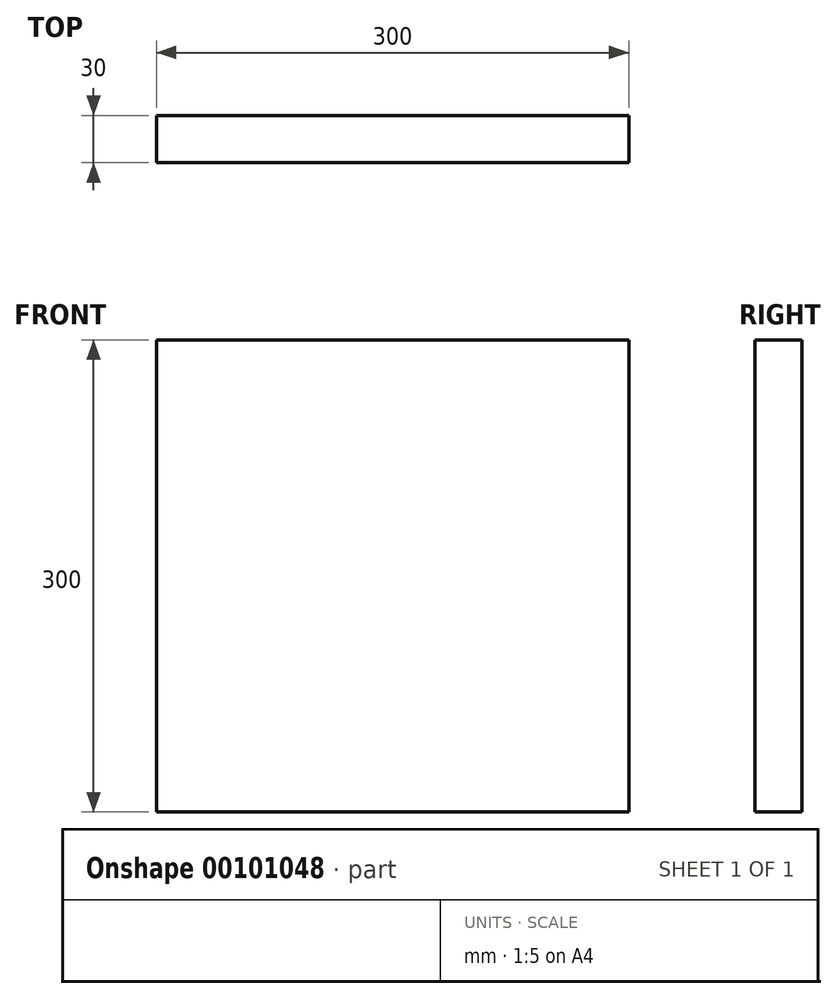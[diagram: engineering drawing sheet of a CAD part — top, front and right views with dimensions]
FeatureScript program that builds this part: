
annotation { "Feature Type Name" : "Feature", "Feature Type Description" : "" }
export const myFeature = defineFeature(function(context is Context, id is Id, definition is map)
    precondition{}
    {
        {
            var Q0;
            Q0=qCreatedBy(makeId("Front.planeOp"),FACE);
            var sketch = newSketch(context, id + "F0", { "sketchPlane" : qUnion([Q0])});
            skLineSegment(sketch, "E0.bottom", {"start": v(-145.6, 145.3) * mm, "end": v(154.4, 145.3) * mm});
            skLineSegment(sketch, "E0.top", {"start": v(-145.6, -154.7) * mm, "end": v(154.4, -154.7) * mm});
            skLineSegment(sketch, "E0.left", {"start": v(-145.6, 145.3) * mm, "end": v(-145.6, -154.7) * mm});
            skLineSegment(sketch, "E0.right", {"start": v(154.4, 145.3) * mm, "end": v(154.4, -154.7) * mm});
            skSolve(sketch);
        }
        {
            var Q0;
            Q0=makeQuery(id+"F0.imprint","IMPRINT",FACE,{"disambiguationData":[TD([[makeQuery(id+"F0.imprint","IMPRINT",EDGE,{"derivedFrom":sQuery(id+"F0.wireOp",EDGE,"E0.bottom")}),-1.0]])]});
            extrude(context, id + "F1", {"entities" : qUnion([Q0]), "endBound" : BoundingType.SYMMETRIC, "depth" : 30 * mm});
        }
    });
